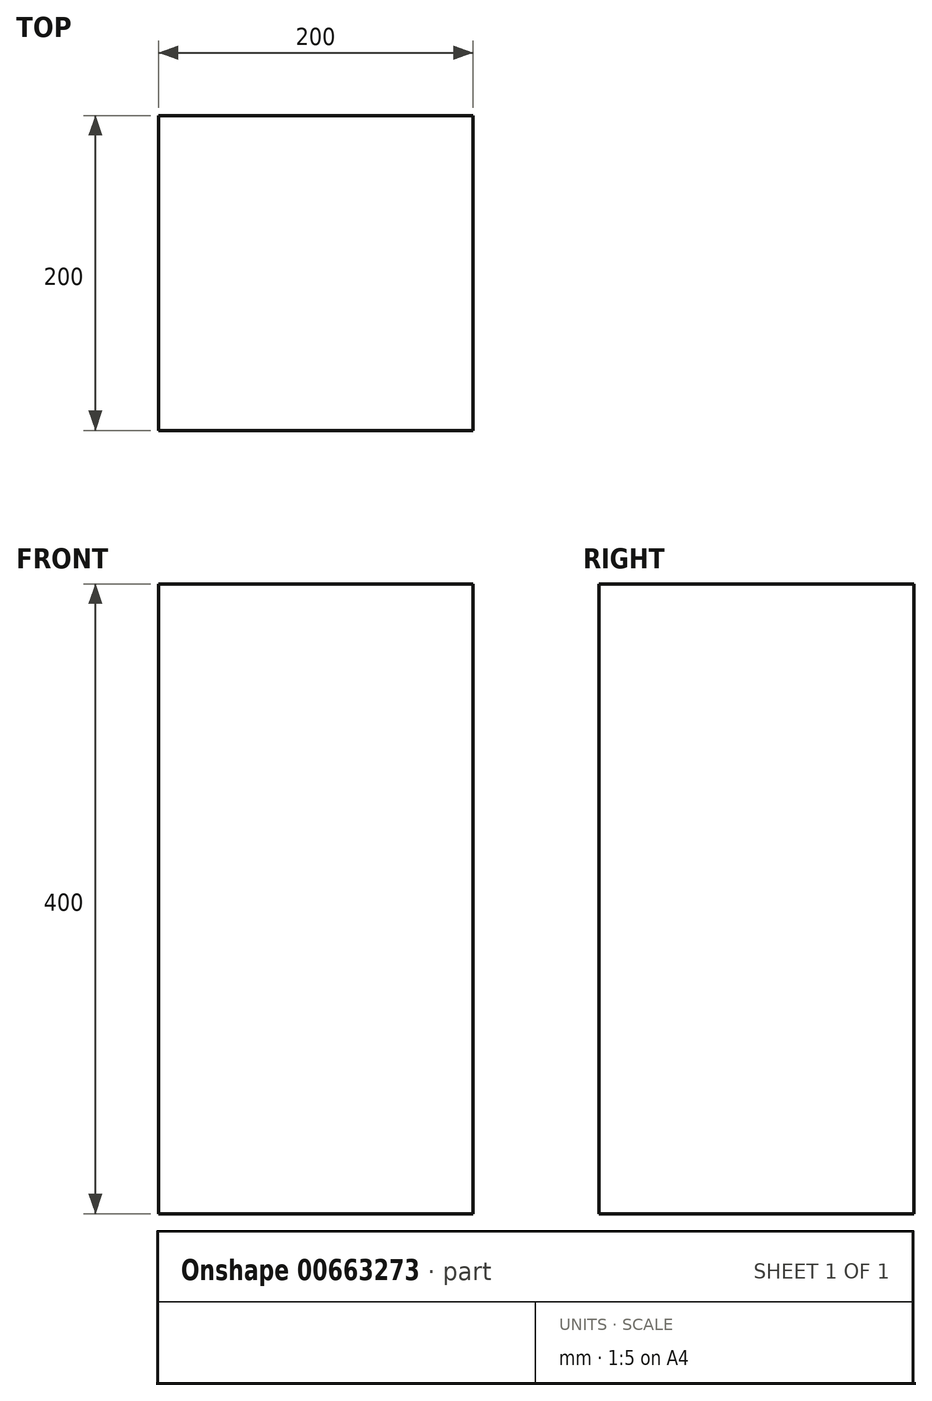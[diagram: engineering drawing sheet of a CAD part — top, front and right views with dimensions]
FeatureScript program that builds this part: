
annotation { "Feature Type Name" : "Feature", "Feature Type Description" : "" }
export const myFeature = defineFeature(function(context is Context, id is Id, definition is map)
    precondition{}
    {
        {
            assignVariable(context, id + "F0", {"name" : "c", "value" : 400});
        }
        {
            var Q0;
            Q0=qCreatedBy(makeId("Top.planeOp"),FACE);
            var sketch = newSketch(context, id + "F1", { "sketchPlane" : qUnion([Q0]) });
            skLineSegment(sketch, "E0.bottom", {"start": v(0, 200) * mm, "end": v(200, 200) * mm});
            skLineSegment(sketch, "E0.top", {"start": v(0, 0) * mm, "end": v(200, 0) * mm});
            skLineSegment(sketch, "E0.left", {"start": v(0, 200) * mm, "end": v(0, 0) * mm});
            skLineSegment(sketch, "E0.right", {"start": v(200, 200) * mm, "end": v(200, 0) * mm});
            skSolve(sketch);
        }
        {
            var Q0;
            Q0=makeQuery(id+"F1.imprint","IMPRINT",FACE,{"disambiguationData":[TD([[makeQuery(id+"F1.imprint","IMPRINT",EDGE,{"derivedFrom":sQuery(id+"F1.wireOp",EDGE,"E0.bottom")}),-1.0]])]});
            extrude(context, id + "F2", {"entities" : qUnion([Q0]), "depth" : (getVariable(context, 'c')) * mm, "offsetDistance" : 25 * mm});
        }
    });
